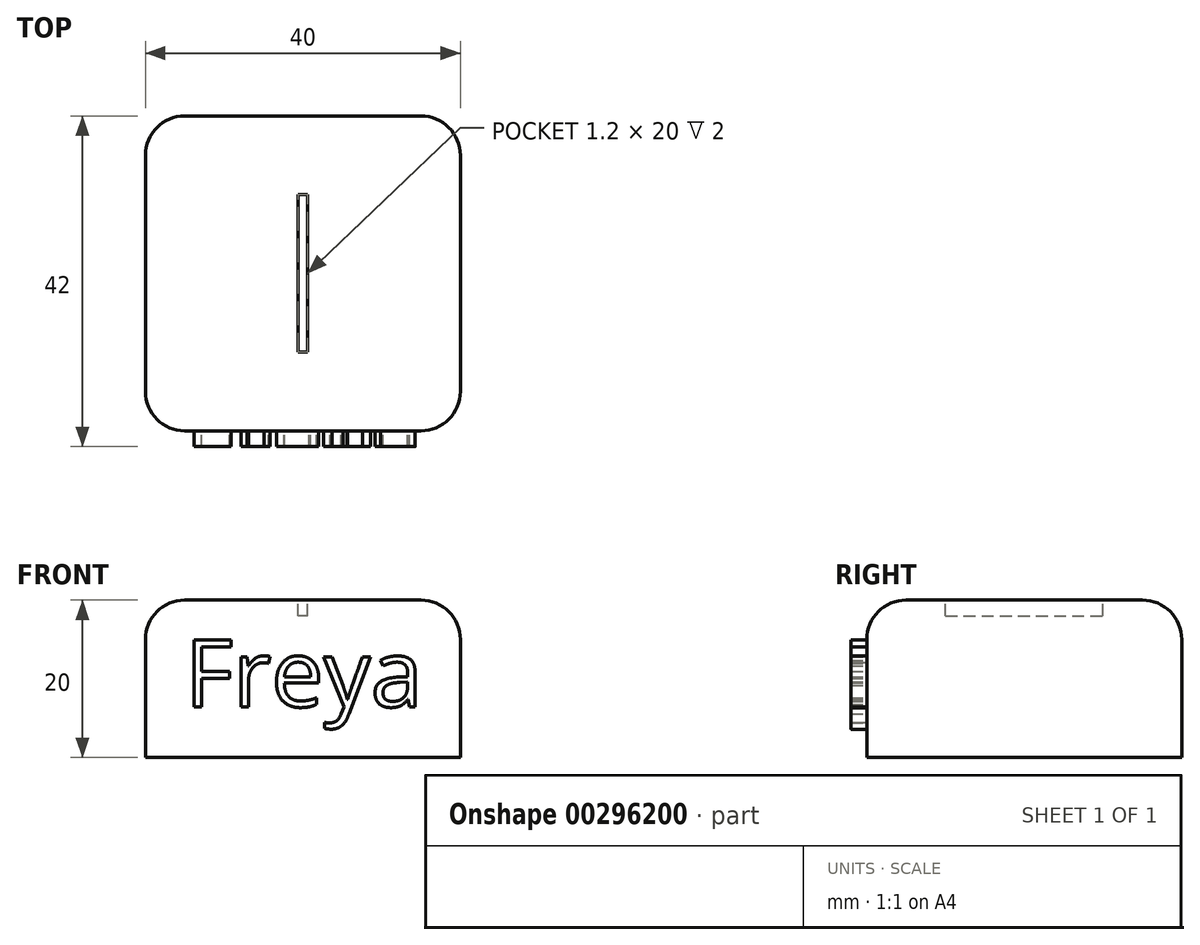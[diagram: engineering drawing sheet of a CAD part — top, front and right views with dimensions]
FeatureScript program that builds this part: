
annotation { "Feature Type Name" : "Feature", "Feature Type Description" : "" }
export const myFeature = defineFeature(function(context is Context, id is Id, definition is map)
    precondition{}
    {
        {
            var Q0;
            Q0=qCreatedBy(makeId("Top.planeOp"),FACE);
            var sketch = newSketch(context, id + "F0", { "sketchPlane" : qUnion([Q0])});
            skLineSegment(sketch, "E0.bottom", {"start": v(20, -20) * mm, "end": v(-20, -20) * mm});
            skLineSegment(sketch, "E0.top", {"start": v(20, 20) * mm, "end": v(-20, 20) * mm});
            skLineSegment(sketch, "E0.left", {"start": v(20, -20) * mm, "end": v(20, 20) * mm});
            skLineSegment(sketch, "E0.right", {"start": v(-20, -20) * mm, "end": v(-20, 20) * mm});
            skPoint(sketch, "E0.middle", {"position": v(0, 0) * mm});
            skLineSegment(sketch, "E1.bottom", {"start": v(0.6, -10) * mm, "end": v(-0.6, -10) * mm});
            skLineSegment(sketch, "E1.top", {"start": v(0.6, 10) * mm, "end": v(-0.6, 10) * mm});
            skLineSegment(sketch, "E1.left", {"start": v(0.6, -10) * mm, "end": v(0.6, 10) * mm});
            skLineSegment(sketch, "E1.right", {"start": v(-0.6, -10) * mm, "end": v(-0.6, 10) * mm});
            skSolve(sketch);
        }
        {
            var Q0;
            Q0=makeQuery(id+"F0.imprint","IMPRINT",FACE,{"disambiguationData":[TD([[makeQuery(id+"F0.imprint","IMPRINT",EDGE,{"derivedFrom":sQuery(id+"F0.wireOp",EDGE,"E0.bottom")}),-1.0]])]});
            var Q1;
            Q1=makeQuery(id+"F0.imprint","IMPRINT",FACE,{"disambiguationData":[TD([[makeQuery(id+"F0.imprint","IMPRINT",EDGE,{"derivedFrom":sQuery(id+"F0.wireOp",EDGE,"E1.bottom")}),-1.0]])]});
            extrude(context, id + "F1", {"entities" : qUnion([Q0, Q1]), "oppositeDirection" : true, "depth" : 20 * mm});
        }
        {
            var Q0;
            Q0=makeQuery(id+"F0.imprint","IMPRINT",FACE,{"disambiguationData":[TD([[makeQuery(id+"F0.imprint","IMPRINT",EDGE,{"derivedFrom":sQuery(id+"F0.wireOp",EDGE,"E1.bottom")}),-1.0]])]});
            extrude(context, id + "F2", {"entities" : qUnion([Q0]), "operationType" : NewBodyOperationType.REMOVE, "oppositeDirection" : true, "depth" : 2 * mm});
        }
        {
            var Q0;
            Q0=makeQuery(id+"F2.boolean.opBoolean","COPY",EDGE,{"derivedFrom":makeQuery(id+"F2.opExtrude","CAP_EDGE",EDGE,{"disambiguationData":[OSD([sQuery(id+"F0.wireOp",EDGE,"E1.left")])],"isStart":true})});
            var Q1;
            Q1=makeQuery(id+"F2.boolean.opBoolean","COPY",EDGE,{"derivedFrom":makeQuery(id+"F2.opExtrude","CAP_EDGE",EDGE,{"disambiguationData":[OSD([sQuery(id+"F0.wireOp",EDGE,"E1.right")])],"isStart":true})});
            var Q2;
            Q2=makeQuery(id+"F1.opExtrude","SWEPT_EDGE",EDGE,{"disambiguationData":[OSD([sQuery(id+"F0.wireOp",EDGE,"E0.bottom"),sQuery(id+"F0.wireOp",EDGE,"E0.left")])]});
            var Q3;
            Q3=makeQuery(id+"F1.opExtrude","SWEPT_EDGE",EDGE,{"disambiguationData":[OSD([sQuery(id+"F0.wireOp",EDGE,"E0.top"),sQuery(id+"F0.wireOp",EDGE,"E0.left")])]});
            var Q4;
            Q4=makeQuery(id+"F1.opExtrude","CAP_EDGE",EDGE,{"disambiguationData":[OSD([sQuery(id+"F0.wireOp",EDGE,"E0.left")])],"isStart":true});
            var Q5;
            Q5=makeQuery(id+"F1.opExtrude","SWEPT_EDGE",EDGE,{"disambiguationData":[OSD([sQuery(id+"F0.wireOp",EDGE,"E0.bottom"),sQuery(id+"F0.wireOp",EDGE,"E0.right")])]});
            var Q6;
            Q6=makeQuery(id+"F1.opExtrude","SWEPT_EDGE",EDGE,{"disambiguationData":[OSD([sQuery(id+"F0.wireOp",EDGE,"E0.top"),sQuery(id+"F0.wireOp",EDGE,"E0.right")])]});
            var Q7;
            Q7=makeQuery(id+"F1.opExtrude","CAP_EDGE",EDGE,{"disambiguationData":[OSD([sQuery(id+"F0.wireOp",EDGE,"E0.top")])],"isStart":true});
            var Q8;
            Q8=makeQuery(id+"F1.opExtrude","CAP_EDGE",EDGE,{"disambiguationData":[OSD([sQuery(id+"F0.wireOp",EDGE,"E0.right")])],"isStart":true});
            var Q9;
            Q9=makeQuery(id+"F1.opExtrude","CAP_EDGE",EDGE,{"disambiguationData":[OSD([sQuery(id+"F0.wireOp",EDGE,"E0.bottom")])],"isStart":true});
            fillet(context, id + "F3", {"entities" : qUnion([Q0, Q1, Q2, Q3, Q4, Q5, Q6, Q7, Q8, Q9]), "radius" : 5 * mm, "tangentPropagation" : true, "allowEdgeOverflow" : false});
        }
        {
            var Q0;
            Q0=makeQuery(id+"F1.opExtrude","SWEPT_FACE",FACE,{"disambiguationData":[OSD([sQuery(id+"F0.wireOp",EDGE,"E0.bottom")])]});
            var sketch = newSketch(context, id + "F4", { "sketchPlane" : qUnion([Q0])});
            skText(sketch, "E2", { "text": "Freya", "fontName": "OpenSans-Regular.ttf"});
            const initialGuessF4  = {"E2": [-0.015, -0.01355, 1, 0, 0.00855]};
            skSetInitialGuess(sketch, initialGuessF4);
            skSolve(sketch);
        }
        {
            var Q0;
            Q0=makeQuery(id+"F4.imprint","IMPRINT",FACE,{"disambiguationData":[TD([[makeQuery(id+"F4.imprint","IMPRINT",EDGE,{"derivedFrom":sQuery(id+"F4.wireOp",EDGE,"E2.sketch_text.stroke-0")}),-1.0]])]});
            var Q1;
            Q1=makeQuery(id+"F4.imprint","IMPRINT",FACE,{"disambiguationData":[TD([[makeQuery(id+"F4.imprint","IMPRINT",EDGE,{"derivedFrom":sQuery(id+"F4.wireOp",EDGE,"E2.sketch_text.stroke-10")}),-1.0]])]});
            var Q2;
            Q2=makeQuery(id+"F4.imprint","IMPRINT",FACE,{"disambiguationData":[TD([[makeQuery(id+"F4.imprint","IMPRINT",EDGE,{"derivedFrom":sQuery(id+"F4.wireOp",EDGE,"E2.sketch_text.stroke-23")}),-1.0]])]});
            var Q3;
            Q3=makeQuery(id+"F4.imprint","IMPRINT",FACE,{"disambiguationData":[TD([[makeQuery(id+"F4.imprint","IMPRINT",EDGE,{"derivedFrom":sQuery(id+"F4.wireOp",EDGE,"E2.sketch_text.stroke-42")}),-1.0]])]});
            var Q4;
            Q4=makeQuery(id+"F4.imprint","IMPRINT",FACE,{"disambiguationData":[TD([[makeQuery(id+"F4.imprint","IMPRINT",EDGE,{"derivedFrom":sQuery(id+"F4.wireOp",EDGE,"E2.sketch_text.stroke-58")}),-1.0]])]});
            extrude(context, id + "F5", {"entities" : qUnion([Q0, Q1, Q2, Q3, Q4]), "operationType" : NewBodyOperationType.ADD, "depth" : 2 * mm});
        }
    });
